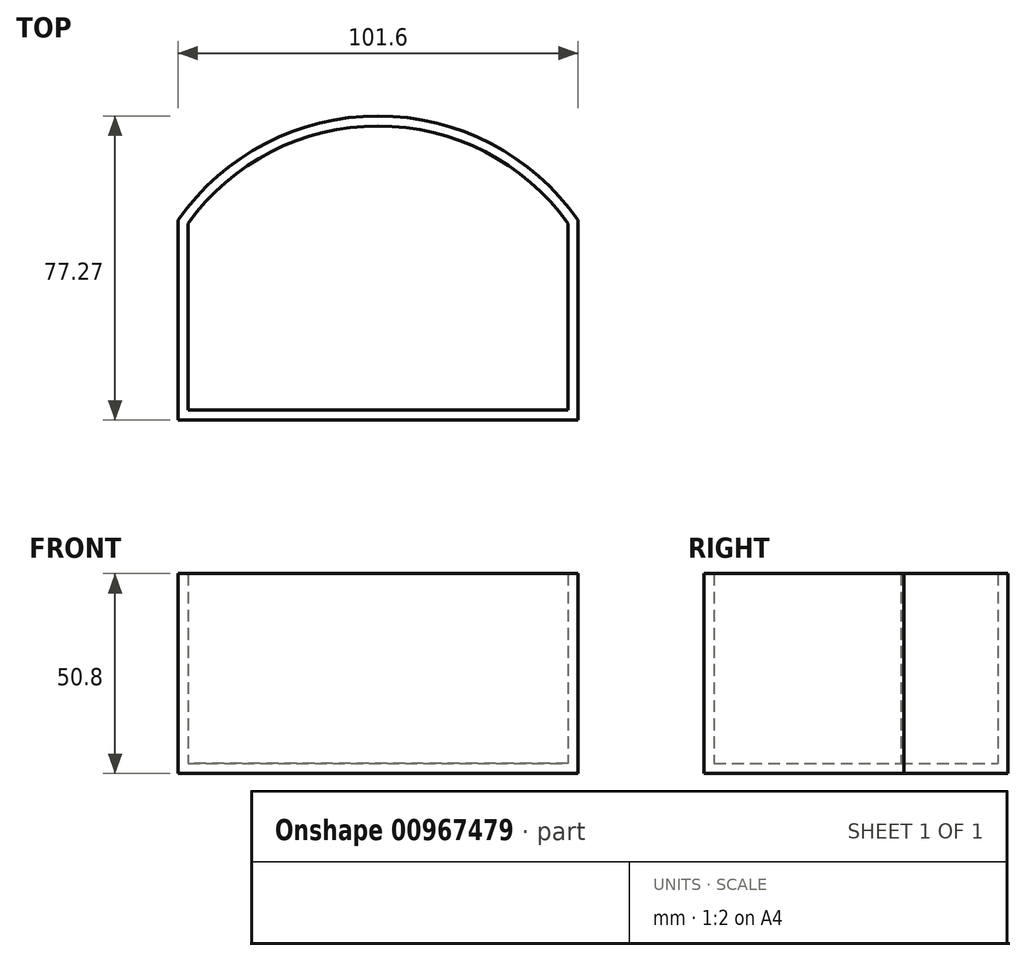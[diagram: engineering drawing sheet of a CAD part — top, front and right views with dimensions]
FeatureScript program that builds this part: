
annotation { "Feature Type Name" : "Feature", "Feature Type Description" : "" }
export const myFeature = defineFeature(function(context is Context, id is Id, definition is map)
    precondition{}
    {
        {
            var Q0;
            Q0=qCreatedBy(makeId("Top.planeOp"),FACE);
            var sketch = newSketch(context, id + "F0", { "sketchPlane" : qUnion([Q0])});
            skLineSegment(sketch, "E0.bottom", {"start": v(-50.8, -25.4) * mm, "end": v(50.8, -25.4) * mm});
            skLineSegment(sketch, "E0.left", {"start": v(-50.8, -25.4) * mm, "end": v(-50.8, 25.4) * mm});
            skLineSegment(sketch, "E0.right", {"start": v(50.8, -25.4) * mm, "end": v(50.8, 25.4) * mm});
            skPoint(sketch, "E0.middle", {"position": v(0, 0) * mm});
            skLineSegment(sketch, "E1", {"start": v(-50.8, 25.4) * mm, "end": v(-50.8, 63.5) * mm, "construction": true});
            skArc(sketch, "E2", {"start": v(50.8, 25.4) * mm, "mid": v(0, 51.87) * mm, "end": v(-50.8, 25.4) * mm});
            skSolve(sketch);
        }
        {
            var Q0;
            Q0 = qSketchRegion(id + "F0", true);
            extrude(context, id + "F1", {"entities" : qUnion([Q0]), "depth" : 50.8 * mm, "offsetDistance" : 25.4 * mm});
        }
        {
            var Q0;
            Q0=makeQuery(id+"F1.opExtrude","CAP_FACE",FACE,{"disambiguationData":[OSD([sQuery(id+"F0.wireOp",EDGE,"E0.bottom"),sQuery(id+"F0.wireOp",EDGE,"E0.left"),sQuery(id+"F0.wireOp",EDGE,"E0.right"),sQuery(id+"F0.wireOp",EDGE,"E2")])],"isStart":false});
            shell(context, id + "F2", {"entities" : qUnion([Q0]), "thickness" : 2.54 * mm});
        }
    });
